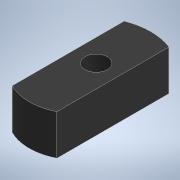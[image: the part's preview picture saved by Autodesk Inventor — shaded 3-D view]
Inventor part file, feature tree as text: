
AUTODESK INVENTOR PART (.ipt)
format: ipt  version: 2021 (Build 250183000, 183)  size: 115,712 bytes
history: native  units: mm
features: extrude x3, sketch x3
ambient origin geometry x8: Origin, YZ Plane, XZ Plane, XY Plane, X Axis, Y Axis, Z Axis, Center Point
bodies: Solid1 (feature_tree)
feature tree (6):
  extrude  "Extrusion1"  Depth=5.0mm
  extrude  "Extrusion3"  Depth=9.0mm
  extrude  "Extrusion4"  Depth=9.0mm
  sketch  "Sketch1"  dims[d0=22.0mm d1=5.0mm]
  sketch  "Sketch2"  dims[d2=9.0mm d3=0.0mm d7=22.5mm]
  sketch  "Sketch3"  dims[d8=11.25mm d9=5.0mm d10=9.0mm d11=0.0mm d12=9.797959mm d13=2.5mm d14=2.5mm d15=11.0mm d16=9.0mm d17=0.0mm]
